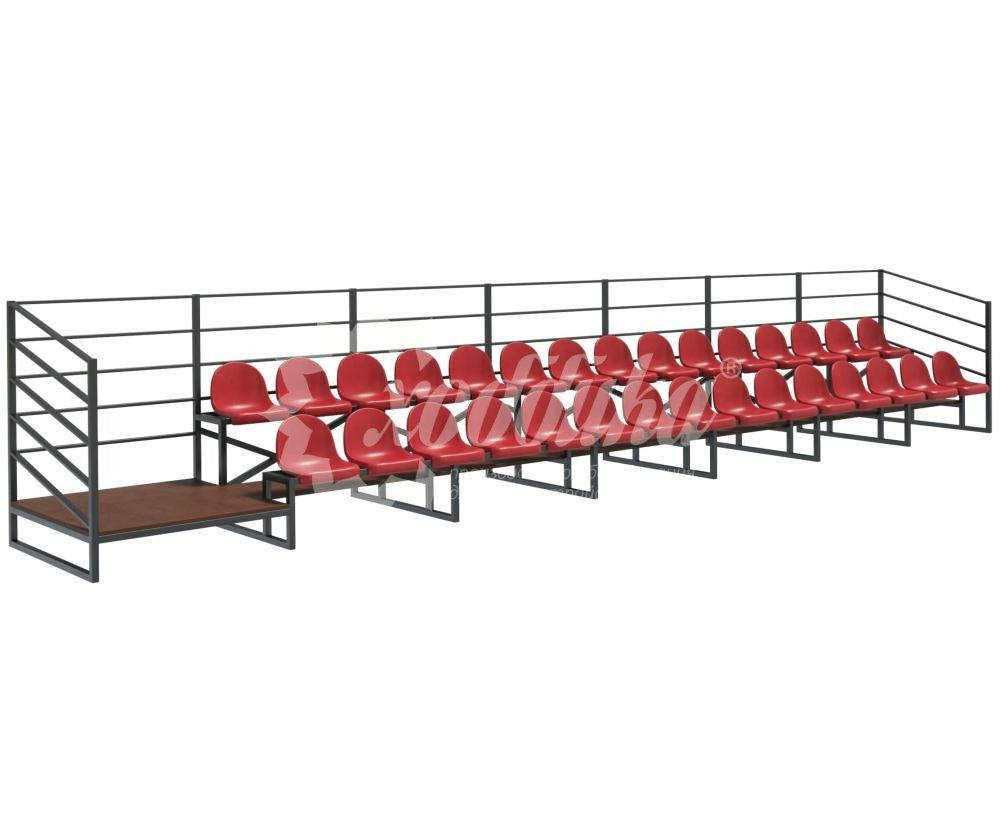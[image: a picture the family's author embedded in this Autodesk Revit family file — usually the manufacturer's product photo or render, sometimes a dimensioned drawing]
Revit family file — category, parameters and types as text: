
# Revit family: 30006 Трибуна двухрядная на 30 мест «Дабл-30» Хоббика
name_source: partatom
category: Антураж
revit_build: Autodesk Revit 2018 (Build: 20180423_1000(x64)
units: mm (PartAtom-declared; Revit-internal decimal feet)

## family parameters
Всегда вертикально = Да
Источник визуального образа = Геометрия семейства
На основе рабочей плоскости = Нет
Общий = Нет
При загрузке вырезать с полостями = Нет
Точка расчета площади = Нет

## types (1)
- Трибуна двухрядная на 30 мест «Дабл-30»
    URL = https://hobbyka.ru
    Артикул товара = Арт 30006
    Высота = 1500 мм
    Группа модели = Мобильные и стационарные трибуны
    Длина = 9030 мм
    Изготовитель = ООО «Хоббика»
    Изображение типоразмера = Трибуна двухрядная на 30 мест «Дабл-30» Арт 30006.jpg
    Материал изделия = Сталь, фанера, пластик
    Описание = Трибуна двухрядная на 30 мест «Дабл-30»
    Цвет каркаса = Сталь
    Цвет настила = Настил
    Цвет сидений = Красный
    Ширина = 1400 мм

## geometry (parser evidence)
native form markers: Blend x418, Sweep x1
no freeform markers — native parametric forms only
